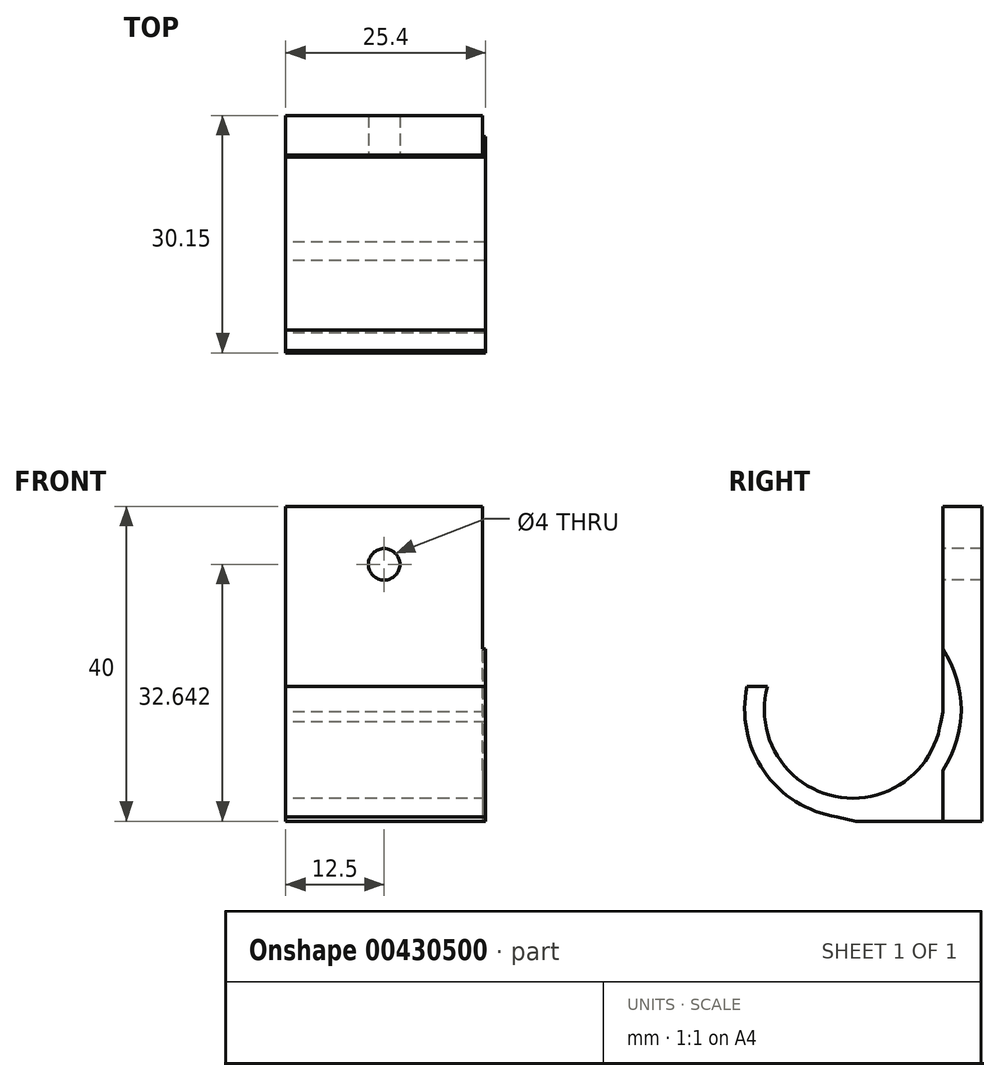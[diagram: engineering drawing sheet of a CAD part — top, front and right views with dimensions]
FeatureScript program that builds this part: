
annotation { "Feature Type Name" : "Feature", "Feature Type Description" : "" }
export const myFeature = defineFeature(function(context is Context, id is Id, definition is map)
    precondition{}
    {
        {
            var Q0;
            Q0=qCreatedBy(makeId("Front.planeOp"),FACE);
            var sketch = newSketch(context, id + "F0", { "sketchPlane" : qUnion([Q0])});
            skLineSegment(sketch, "E0.bottom", {"start": v(12.5, 20) * mm, "end": v(-12.5, 20) * mm});
            skLineSegment(sketch, "E0.top", {"start": v(12.5, -20) * mm, "end": v(-12.5, -20) * mm});
            skLineSegment(sketch, "E0.left", {"start": v(12.5, 20) * mm, "end": v(12.5, -20) * mm});
            skLineSegment(sketch, "E0.right", {"start": v(-12.5, 20) * mm, "end": v(-12.5, -20) * mm});
            skPoint(sketch, "E0.middle", {"position": v(0, 0) * mm});
            skSolve(sketch);
        }
        {
            var Q0;
            Q0=makeQuery(id+"F0.imprint","IMPRINT",FACE,{"disambiguationData":[TD([[makeQuery(id+"F0.imprint","IMPRINT",EDGE,{"derivedFrom":sQuery(id+"F0.wireOp",EDGE,"E0.bottom")}),1.0]])]});
            extrude(context, id + "F1", {"entities" : qUnion([Q0]), "depth" : 5 * mm});
        }
        {
            var Q0;
            Q0=makeQuery(id+"F1.opExtrude","SWEPT_FACE",FACE,{"disambiguationData":[OSD([sQuery(id+"F0.wireOp",EDGE,"E0.right")])]});
            var sketch = newSketch(context, id + "F2", { "sketchPlane" : qUnion([Q0])});
            skCircle(sketch, "E1", {"center": v(16.4, -5.82) * mm, "radius": 11.25 * mm});
            skSolve(sketch);
        }
        {
            var Q0;
            {var subQ0=sQuery(id+"F0.wireOp",EDGE,"E0.right");Q0=makeQuery(id+"F2.imprint","IMPRINT",FACE,{"disambiguationData":[TD([[makeQuery(id+"F2.imprint","IMPRINT",EDGE,{"derivedFrom":makeQuery(id+"F1.opExtrude","CAP_EDGE",EDGE,{"disambiguationData":[OSD([subQ0])],"isStart":true})}),1.0]])]});}
            var sketch = newSketch(context, id + "F3", { "sketchPlane" : qUnion([Q0])});
            skCircle(sketch, "E2", {"center": v(16.4, -5.82) * mm, "radius": 13.75 * mm});
            skSolve(sketch);
        }
        {
            var Q0;
            {var subQ0=sQuery(id+"F0.wireOp",EDGE,"E0.right");Q0=makeQuery(id+"F2.imprint","IMPRINT",FACE,{"disambiguationData":[TD([[makeQuery(id+"F2.imprint","IMPRINT",EDGE,{"derivedFrom":makeQuery(id+"F1.opExtrude","CAP_EDGE",EDGE,{"disambiguationData":[OSD([subQ0])],"isStart":true})}),1.0]])]});}
            var sketch = newSketch(context, id + "F4", { "sketchPlane" : qUnion([Q0])});
            skLineSegment(sketch, "E3", {"start": v(27.32, -2.83) * mm, "end": v(30.1, -2.83) * mm});
            skSolve(sketch);
        }
        {
            var Q0;
            {var subQ0=sQuery(id+"F0.wireOp",EDGE,"E0.right");Q0=makeQuery(id+"F2.imprint","IMPRINT",FACE,{"disambiguationData":[TD([[makeQuery(id+"F2.imprint","IMPRINT",EDGE,{"derivedFrom":makeQuery(id+"F1.opExtrude","CAP_EDGE",EDGE,{"disambiguationData":[OSD([subQ0])],"isStart":true})}),1.0]])]});}
            var sketch = newSketch(context, id + "F5", { "sketchPlane" : qUnion([Q0])});
            skLineSegment(sketch, "E4", {"start": v(4.99, -6.13) * mm, "end": v(5.43, -8.37) * mm});
            skSolve(sketch);
        }
        {
            var Q0;
            {var subQ0=sQuery(id+"F3.wireOp",EDGE,"E2");var subQ1=makeQuery(id+"F2.imprint","IMPRINT",EDGE,{"derivedFrom":makeQuery(id+"F1.opExtrude","CAP_EDGE",EDGE,{"disambiguationData":[OSD([sQuery(id+"F0.wireOp",EDGE,"E0.right")])],"isStart":false})});var subQ2=makeQuery(id+"F3.imprint","INTERSECT",VERTEX,{"disambiguationData":[OD(0.0)],"derivedFrom":[subQ1,subQ0]});Q0=makeQuery(id+"F3.imprint","IMPRINT",FACE,{"disambiguationData":[TD([[makeQuery(id+"F3.imprint","IMPRINT",EDGE,{"disambiguationData":[TD([[subQ2,1.0]])],"derivedFrom":subQ0}),1.0]])]});}
            var Q1;
            Q1 = qSketchRegion(id + "FqXUiDtsP3dSqE7_1", true);
            var Q2;
            Q2 = qSketchRegion(id + "F4", true);
            extrude(context, id + "F6", {"entities" : qUnion([Q0, Q1, Q2]), "operationType" : NewBodyOperationType.ADD, "depth" : -25.4 * mm});
        }
        {
            var Q0;
            Q0 = qSketchRegion(id + "F3", true);
            extrude(context, id + "F7", {"entities" : qUnion([Q0]), "operationType" : NewBodyOperationType.ADD, "depth" : -25.4 * mm});
        }
        {
            var Q0;
            {var subQ0=sQuery(id+"F0.wireOp",EDGE,"E0.right");Q0=makeQuery(id+"F2.imprint","IMPRINT",FACE,{"disambiguationData":[TD([[makeQuery(id+"F2.imprint","IMPRINT",EDGE,{"derivedFrom":makeQuery(id+"F1.opExtrude","CAP_EDGE",EDGE,{"disambiguationData":[OSD([subQ0])],"isStart":true})}),1.0]])]});}
            var sketch = newSketch(context, id + "F8", { "sketchPlane" : qUnion([Q0])});
            skLineSegment(sketch, "E5", {"start": v(4.94, -19.99) * mm, "end": v(16.05, -19.99) * mm});
            skLineSegment(sketch, "E6", {"start": v(16.05, -19.99) * mm, "end": v(19.54, -19.16) * mm});
            skLineSegment(sketch, "E7", {"start": v(19.54, -19.16) * mm, "end": v(7.04, -15.23) * mm});
            skLineSegment(sketch, "E8", {"start": v(7.04, -15.23) * mm, "end": v(4.52, -12.22) * mm});
            skLineSegment(sketch, "E9", {"start": v(4.52, -12.22) * mm, "end": v(4.94, -20.15) * mm});
            skSolve(sketch);
        }
        {
            var Q0;
            {var subQ4=sQuery(id+"F8.wireOp",EDGE,"E6");Q0=makeQuery(id+"F8.imprint","IMPRINT",FACE,{"disambiguationData":[TD([[makeQuery(id+"F8.imprint","IMPRINT",EDGE,{"derivedFrom":subQ4}),1.0]])]});}
            extrude(context, id + "F9", {"entities" : qUnion([Q0]), "operationType" : NewBodyOperationType.ADD, "depth" : -25.4 * mm});
        }
        {
            var Q0;
            Q0=makeQuery(id+"F2.imprint","IMPRINT",FACE,{"disambiguationData":[TD([[makeQuery(id+"F2.imprint","IMPRINT",EDGE,{"derivedFrom":sQuery(id+"F2.wireOp",EDGE,"E1")}),1.0]])]});
            extrude(context, id + "F10", {"entities" : qUnion([Q0]), "operationType" : NewBodyOperationType.REMOVE, "oppositeDirection" : true, "depth" : 25.4 * mm});
        }
        {
            var Q0;
            {var subQ0=sQuery(id+"F0.wireOp",EDGE,"E0.right");Q0=makeQuery(id+"F5.imprint","IMPRINT",FACE,{"disambiguationData":[TD([[makeQuery(id+"F5.imprint","IMPRINT",EDGE,{"derivedFrom":makeQuery(id+"F2.imprint","IMPRINT",EDGE,{"derivedFrom":makeQuery(id+"F1.opExtrude","CAP_EDGE",EDGE,{"disambiguationData":[OSD([subQ0])],"isStart":true})})}),1.0]])]});}
            var sketch = newSketch(context, id + "F11", { "sketchPlane" : qUnion([Q0])});
            skLineSegment(sketch, "E10", {"start": v(5, 3.56) * mm, "end": v(5, -6.12) * mm});
            skLineSegment(sketch, "E11", {"start": v(5, -6.12) * mm, "end": v(5.35, -7.8) * mm});
            skLineSegment(sketch, "E12", {"start": v(5.35, -7.8) * mm, "end": v(19.81, -7.8) * mm});
            skLineSegment(sketch, "E13", {"start": v(19.81, -7.8) * mm, "end": v(20.63, -2.88) * mm});
            skLineSegment(sketch, "E14", {"start": v(20.63, -2.88) * mm, "end": v(33.69, -2.88) * mm});
            skLineSegment(sketch, "E15", {"start": v(33.69, -2.88) * mm, "end": v(32.5, 10.76) * mm});
            skLineSegment(sketch, "E16", {"start": v(32.5, 10.76) * mm, "end": v(12.17, 13.46) * mm});
            skLineSegment(sketch, "E17", {"start": v(12.17, 13.46) * mm, "end": v(5, 3.56) * mm});
            skSolve(sketch);
        }
        {
            var Q0;
            {var subQ5=sQuery(id+"F11.wireOp",EDGE,"E12");Q0=makeQuery(id+"F11.imprint","IMPRINT",FACE,{"disambiguationData":[TD([[makeQuery(id+"F11.imprint","IMPRINT",EDGE,{"derivedFrom":subQ5}),1.0]])]});}
            extrude(context, id + "F12", {"entities" : qUnion([Q0]), "operationType" : NewBodyOperationType.REMOVE, "oppositeDirection" : true, "depth" : 25.4 * mm});
        }
        {
            var Q0;
            {var subQ0=sQuery(id+"F0.wireOp",EDGE,"E0.right");var subQ2=sQuery(id+"F0.wireOp",EDGE,"E0.left");var subQ3=sQuery(id+"F0.wireOp",EDGE,"E0.bottom");Q0=makeQuery(id+"F12.boolean.opBoolean","MERGE",FACE,{"derivedFrom":[makeQuery(id+"F6.boolean.opBoolean","SPLIT",FACE,{"disambiguationData":[TD([makeQuery(id+"F1.opExtrude","SWEPT_FACE",FACE,{"disambiguationData":[OSD([subQ3])]})])],"derivedFrom":makeQuery(id+"F1.opExtrude","CAP_FACE",FACE,{"disambiguationData":[OSD([subQ3,sQuery(id+"F0.wireOp",EDGE,"E0.top"),subQ2,subQ0])],"isStart":false})}),makeQuery(id+"F12.opExtrude","SWEPT_FACE",FACE,{"disambiguationData":[OSD([subQ0])]})]});}
            var sketch = newSketch(context, id + "F13", { "sketchPlane" : qUnion([Q0])});
            skCircle(sketch, "E18", {"center": v(0, 12.64) * mm, "radius": 2 * mm});
            skSolve(sketch);
        }
        {
            var Q0;
            Q0=makeQuery(id+"F13.imprint","IMPRINT",FACE,{"disambiguationData":[TD([[makeQuery(id+"F13.imprint","IMPRINT",EDGE,{"derivedFrom":sQuery(id+"F13.wireOp",EDGE,"E18")}),1.0]])]});
            extrude(context, id + "F14", {"entities" : qUnion([Q0]), "operationType" : NewBodyOperationType.REMOVE, "oppositeDirection" : true, "depth" : 25.4 * mm});
        }
    });
